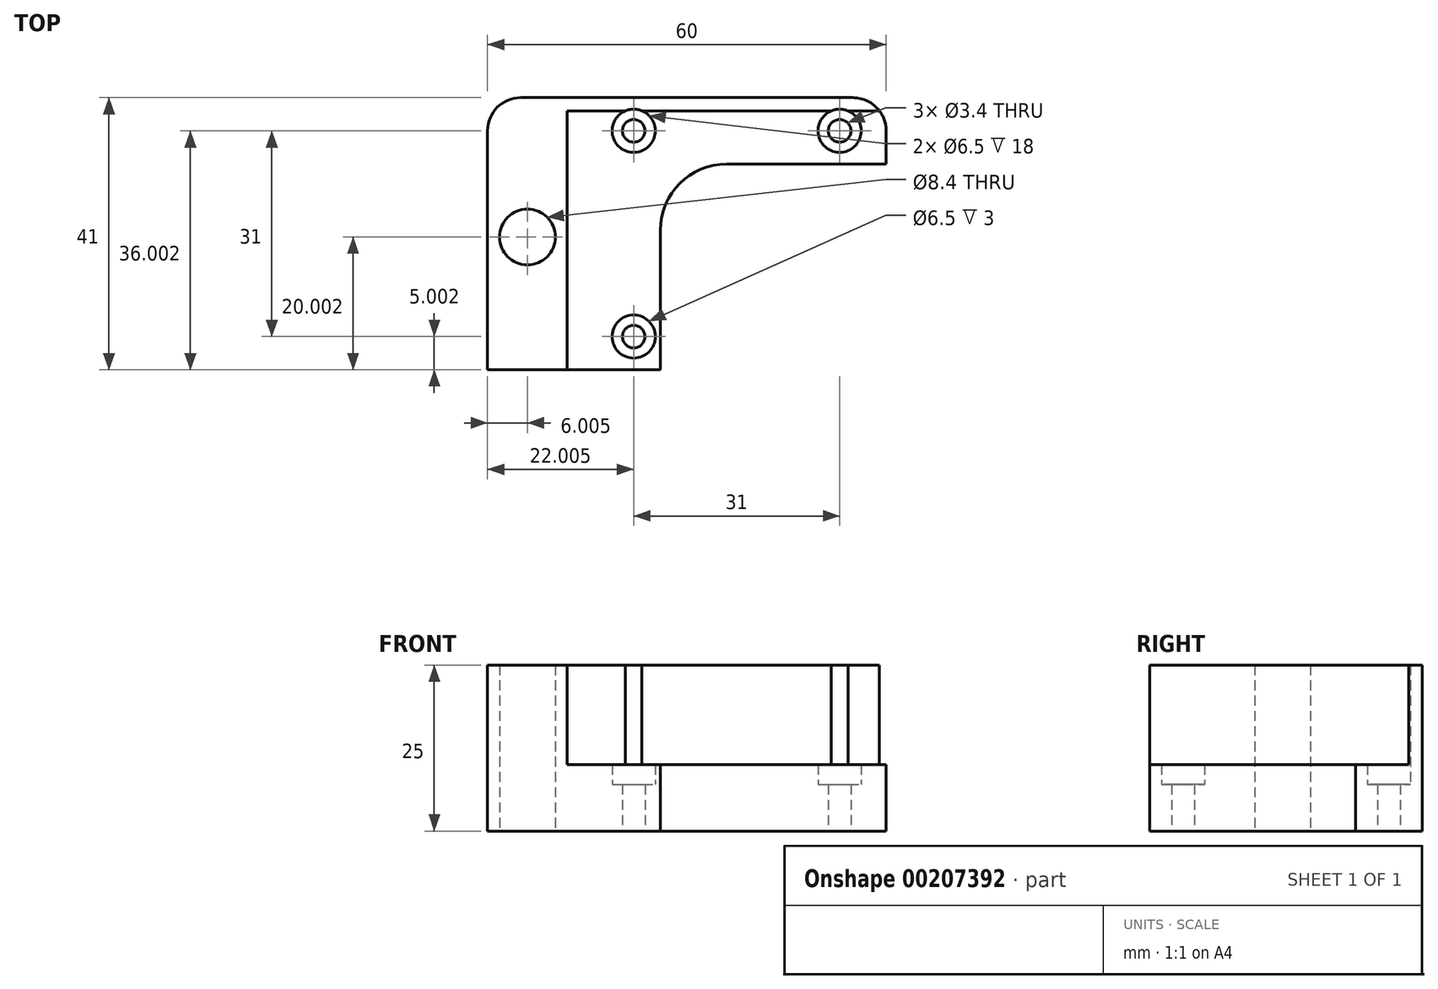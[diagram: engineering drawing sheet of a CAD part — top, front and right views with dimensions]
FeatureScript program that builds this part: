
annotation { "Feature Type Name" : "Feature", "Feature Type Description" : "" }
export const myFeature = defineFeature(function(context is Context, id is Id, definition is map)
    precondition{}
    {
        {
            var Q0;
            Q0=qCreatedBy(makeId("Top.planeOp"),FACE);
            var sketch = newSketch(context, id + "F0", { "sketchPlane" : qUnion([Q0])});
            skLineSegment(sketch, "E0", {"start": v(-65.12, -50.59) * mm, "end": v(-77.12, -50.59) * mm});
            skLineSegment(sketch, "E1", {"start": v(-77.12, -50.59) * mm, "end": v(-77.12, -11.59) * mm});
            skLineSegment(sketch, "E2", {"start": v(-65.12, -11.59) * mm, "end": v(-77.12, -11.59) * mm});
            skLineSegment(sketch, "E3", {"start": v(-65.12, -11.59) * mm, "end": v(-65.12, -50.59) * mm});
            skLineSegment(sketch, "E4", {"start": v(-55.12, -14.59) * mm, "end": v(-24.12, -45.59) * mm, "construction": true});
            skCircle(sketch, "E5", {"center": v(-39.62, -30.09) * mm, "radius": 11 * mm, "construction": true});
            skCircle(sketch, "E6", {"center": v(-71.12, -30.59) * mm, "radius": 4.2 * mm});
            skPoint(sketch, "E7", {"position": v(-71.12, -11.59) * mm});
            skLineSegment(sketch, "E8.top", {"start": v(-77.12, -9.59) * mm, "end": v(-17.12, -9.59) * mm});
            skLineSegment(sketch, "E8.left", {"start": v(-77.12, -11.59) * mm, "end": v(-77.12, -9.59) * mm});
            skLineSegment(sketch, "E9", {"start": v(-51.12, -41.59) * mm, "end": v(-51.12, -19.59) * mm});
            skLineSegment(sketch, "E10", {"start": v(-51.12, -19.59) * mm, "end": v(-17.12, -19.59) * mm});
            skLineSegment(sketch, "E11", {"start": v(-17.12, -19.59) * mm, "end": v(-17.12, -9.59) * mm});
            skPoint(sketch, "E12", {"position": v(-55.12, -14.59) * mm});
            skPoint(sketch, "E13", {"position": v(-55.12, -45.59) * mm});
            skPoint(sketch, "E14", {"position": v(-24.12, -45.59) * mm});
            skPoint(sketch, "E15", {"position": v(-24.12, -14.59) * mm});
            skLineSegment(sketch, "E16", {"start": v(-51.12, -41.59) * mm, "end": v(-51.12, -50.59) * mm});
            skLineSegment(sketch, "E17", {"start": v(-65.12, -50.59) * mm, "end": v(-51.12, -50.59) * mm});
            skLineSegment(sketch, "E18", {"start": v(-65.12, -11.59) * mm, "end": v(-17.12, -11.59) * mm});
            skSolve(sketch);
        }
        {
            var Q0;
            Q0=makeQuery(id+"F0.imprint","IMPRINT",FACE,{"disambiguationData":[TD([[makeQuery(id+"F0.imprint","IMPRINT",EDGE,{"derivedFrom":sQuery(id+"F0.wireOp",EDGE,"E3")}),1.0]])]});
            extrude(context, id + "F1", {"entities" : qUnion([Q0]), "depth" : 10 * mm, "offsetDistance" : 25 * mm});
        }
        {
            var Q0;
            Q0=makeQuery(id+"F0.imprint","IMPRINT",FACE,{"disambiguationData":[TD([[makeQuery(id+"F0.imprint","IMPRINT",EDGE,{"derivedFrom":sQuery(id+"F0.wireOp",EDGE,"E0")}),-1.0]])]});
            var Q1;
            Q1=makeQuery(id+"F0.imprint","IMPRINT",FACE,{"disambiguationData":[TD([[makeQuery(id+"F0.imprint","IMPRINT",EDGE,{"derivedFrom":sQuery(id+"F0.wireOp",EDGE,"E2")}),-1.0]])]});
            extrude(context, id + "F2", {"entities" : qUnion([Q0, Q1]), "operationType" : NewBodyOperationType.ADD, "depth" : 25 * mm, "offsetDistance" : 25 * mm});
        }
        {
            var Q0;
            Q0=makeQuery(id+"F2.opExtrude","SWEPT_EDGE",EDGE,{"disambiguationData":[OSD([sQuery(id+"F0.wireOp",EDGE,"E8.top"),sQuery(id+"F0.wireOp",EDGE,"E8.left")])]});
            var Q1;
            Q1=makeQuery(id+"F2.opExtrude","SWEPT_EDGE",EDGE,{"disambiguationData":[OSD([sQuery(id+"F0.wireOp",EDGE,"E8.top"),sQuery(id+"F0.wireOp",EDGE,"E11")])]});
            fillet(context, id + "F3", {"entities" : qUnion([Q0, Q1]), "radius" : 5 * mm, "tangentPropagation" : true, "allowEdgeOverflow" : false});
        }
        {
            var Q0;
            Q0=makeQuery(id+"F1.opExtrude","CAP_FACE",FACE,{"disambiguationData":[OSD([sQuery(id+"F0.wireOp",EDGE,"E3"),sQuery(id+"F0.wireOp",EDGE,"E9"),sQuery(id+"F0.wireOp",EDGE,"E10"),sQuery(id+"F0.wireOp",EDGE,"E11"),sQuery(id+"F0.wireOp",EDGE,"E16"),sQuery(id+"F0.wireOp",EDGE,"E17"),sQuery(id+"F0.wireOp",EDGE,"E18")])],"isStart":false});
            var sketch = newSketch(context, id + "F4", { "sketchPlane" : qUnion([Q0])});
            skPoint(sketch, "E19.0", {"position": v(-55.12, -14.59) * mm});
            skPoint(sketch, "E20.0", {"position": v(-24.12, -14.59) * mm});
            skPoint(sketch, "E21.0", {"position": v(-55.12, -45.59) * mm});
            skSolve(sketch);
        }
        {
            var Q0;
            Q0=sQuery(id+"F4.wireOp",VERTEX,"E21.0");
            var Q1;
            Q1=sQuery(id+"F4.wireOp",VERTEX,"E19.0");
            var Q2;
            Q2=sQuery(id+"F4.wireOp",VERTEX,"E20.0");
            var Q3;
            Q3=makeQuery(id+"F1.opExtrude","SWEPT_BODY",BODY,{"disambiguationData":[OSD([sQuery(id+"F0.wireOp",EDGE,"E3"),sQuery(id+"F0.wireOp",EDGE,"E9"),sQuery(id+"F0.wireOp",EDGE,"E10"),sQuery(id+"F0.wireOp",EDGE,"E11"),sQuery(id+"F0.wireOp",EDGE,"E16"),sQuery(id+"F0.wireOp",EDGE,"E17"),sQuery(id+"F0.wireOp",EDGE,"E18")])]});
            hole(context, id + "F5", {"style" : HoleStyle.C_BORE, "endStyle" : HoleEndStyle.THROUGH, "standardTappedOrClearance" : lookupTablePath({ "fit" : "Normal", "standard" : "ISO", "size" : "M3", "type" : "Clearance" }), "standardBlindInLast" : lookupTablePath({ "fit" : "Normal", "standard" : "ISO", "engagement" : "75%", "pitch" : "0.5 mm", "size" : "M3", "type" : "Clearance & tapped" }), "holeDiameter" : 3.4 * mm, "cBoreDiameter" : 6.5 * mm, "cBoreDepth" : 3 * mm, "majorDiameter" : 5 * mm, "isTappedThrough" : true, "tappedDepth" : 12 * mm, "tapClearance" : 3, "locations" : qUnion([Q0, Q1, Q2]), "scope" : qUnion([Q3]), "startStyle" : HoleStartStyle.SKETCH});
        }
        {
            var Q0;
            Q0=makeQuery(id+"F1.opExtrude","SWEPT_EDGE",EDGE,{"disambiguationData":[OSD([sQuery(id+"F0.wireOp",EDGE,"E9"),sQuery(id+"F0.wireOp",EDGE,"E10")])]});
            fillet(context, id + "F6", {"entities" : qUnion([Q0]), "radius" : 10 * mm, "tangentPropagation" : true, "allowEdgeOverflow" : false});
        }
    });
